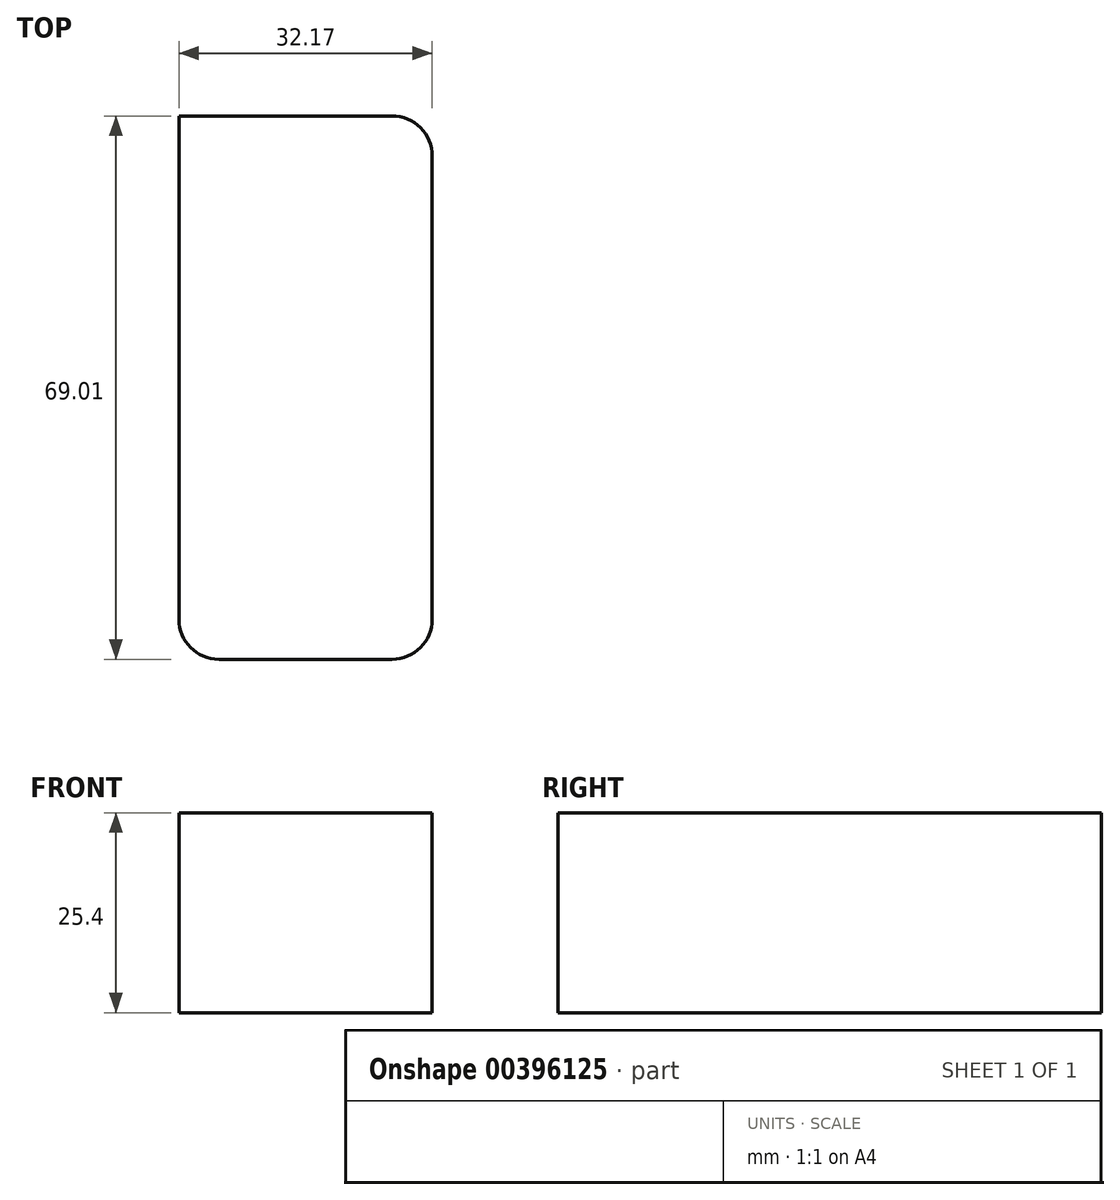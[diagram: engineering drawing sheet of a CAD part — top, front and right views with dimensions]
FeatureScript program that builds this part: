
annotation { "Feature Type Name" : "Feature", "Feature Type Description" : "" }
export const myFeature = defineFeature(function(context is Context, id is Id, definition is map)
    precondition{}
    {
        {
            var Q0;
            Q0=qCreatedBy(makeId("Top.planeOp"),FACE);
            var sketch = newSketch(context, id + "F0", { "sketchPlane" : qUnion([Q0])});
            skLineSegment(sketch, "E0.bottom", {"start": v(-8.97, -22.78) * mm, "end": v(-41.14, -22.78) * mm});
            skLineSegment(sketch, "E0.top", {"start": v(-8.97, 46.23) * mm, "end": v(-41.14, 46.23) * mm});
            skLineSegment(sketch, "E0.left", {"start": v(-8.97, -22.78) * mm, "end": v(-8.97, 46.23) * mm});
            skLineSegment(sketch, "E0.right", {"start": v(-41.14, -22.78) * mm, "end": v(-41.14, 46.23) * mm});
            skSolve(sketch);
        }
        {
            var Q0;
            Q0=makeQuery(id+"F0.imprint","IMPRINT",FACE,{"disambiguationData":[TD([[makeQuery(id+"F0.imprint","IMPRINT",EDGE,{"derivedFrom":sQuery(id+"F0.wireOp",EDGE,"E0.bottom")}),-1.0]])]});
            extrude(context, id + "F1", {"entities" : qUnion([Q0]), "depth" : 25.4 * mm});
        }
        {
            var Q0;
            Q0=makeQuery(id+"F1.opExtrude","SWEPT_EDGE",EDGE,{"disambiguationData":[OSD([sQuery(id+"F0.wireOp",EDGE,"E0.bottom"),sQuery(id+"F0.wireOp",EDGE,"E0.left")])]});
            var Q1;
            Q1=makeQuery(id+"F1.opExtrude","SWEPT_EDGE",EDGE,{"disambiguationData":[OSD([sQuery(id+"F0.wireOp",EDGE,"E0.top"),sQuery(id+"F0.wireOp",EDGE,"E0.left")])]});
            var Q2;
            Q2=makeQuery(id+"F1.opExtrude","SWEPT_EDGE",EDGE,{"disambiguationData":[OSD([sQuery(id+"F0.wireOp",EDGE,"E0.bottom"),sQuery(id+"F0.wireOp",EDGE,"E0.right")])]});
            fillet(context, id + "F2", {"entities" : qUnion([Q0, Q1, Q2]), "radius" : 5.08 * mm, "tangentPropagation" : true, "allowEdgeOverflow" : false});
        }
    });
